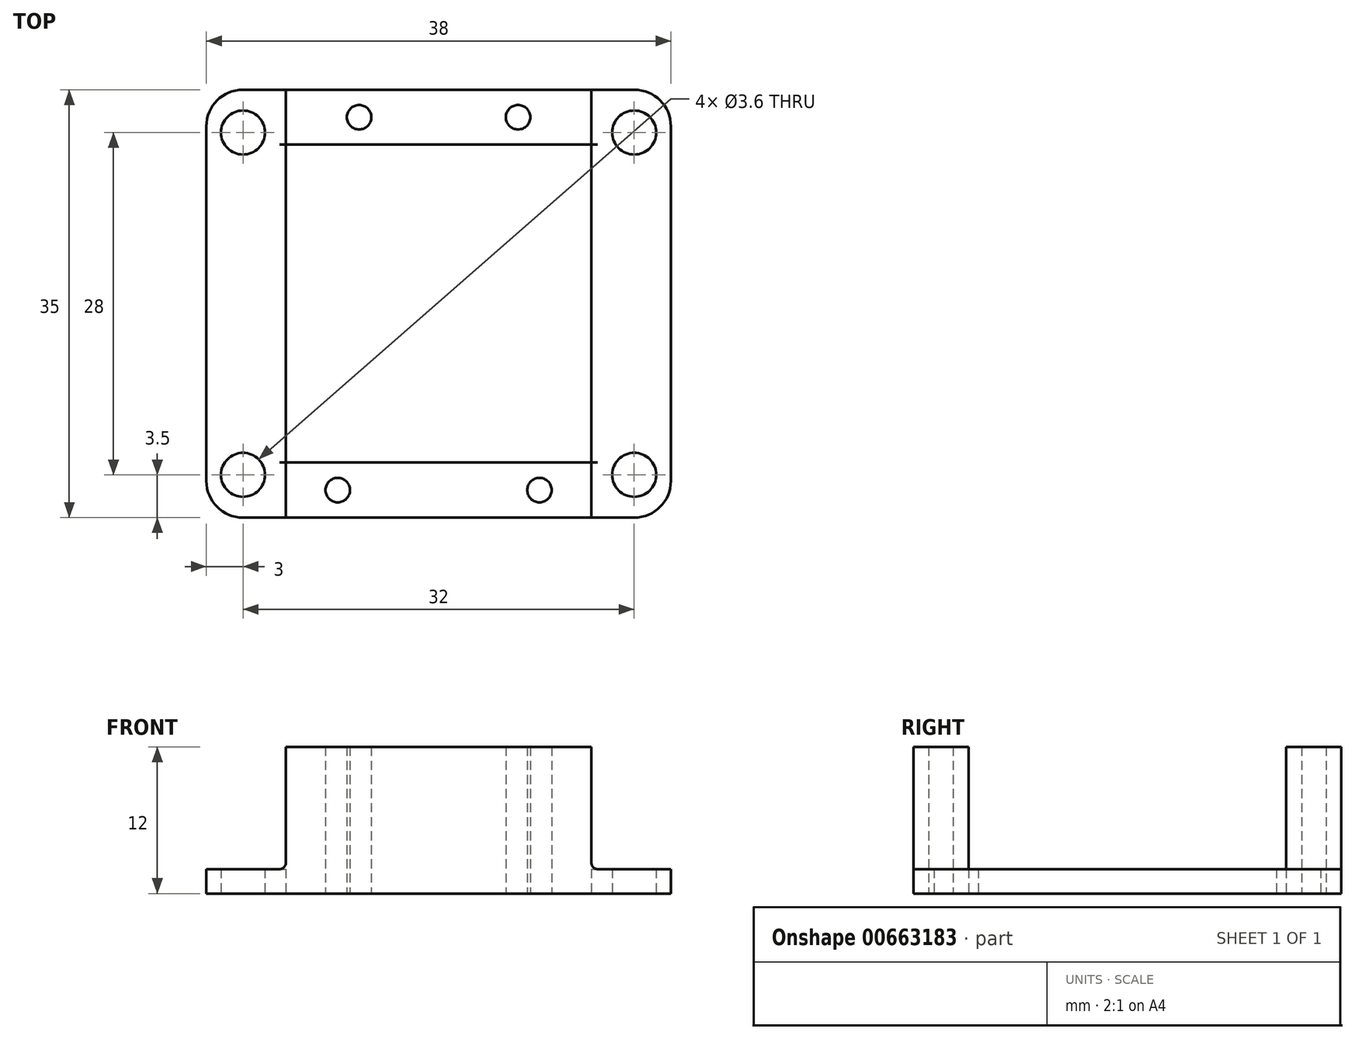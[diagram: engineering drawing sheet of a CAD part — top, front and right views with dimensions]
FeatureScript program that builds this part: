
annotation { "Feature Type Name" : "Feature", "Feature Type Description" : "" }
export const myFeature = defineFeature(function(context is Context, id is Id, definition is map)
    precondition{}
    {
        {
            var Q0;
            Q0=qCreatedBy(makeId("Top.planeOp"),FACE);
            var sketch = newSketch(context, id + "F0", { "sketchPlane" : qUnion([Q0])});
            skLineSegment(sketch, "E0.bottom", {"start": v(-19, 17.5) * mm, "end": v(19, 17.5) * mm});
            skLineSegment(sketch, "E0.top", {"start": v(-19, -17.5) * mm, "end": v(19, -17.5) * mm});
            skLineSegment(sketch, "E0.left", {"start": v(-19, 17.5) * mm, "end": v(-19, -17.5) * mm});
            skLineSegment(sketch, "E0.right", {"start": v(19, 17.5) * mm, "end": v(19, -17.5) * mm});
            skCircle(sketch, "E1", {"center": v(-16, 14) * mm, "radius": 1.8 * mm});
            skCircle(sketch, "E2.MirrorC", {"center": v(16, 14) * mm, "radius": 1.8 * mm});
            skCircle(sketch, "E3.MirrorC", {"center": v(-16, -14) * mm, "radius": 1.8 * mm});
            skCircle(sketch, "E4.MirrorC", {"center": v(16, -14) * mm, "radius": 1.8 * mm});
            skCircle(sketch, "E5", {"center": v(-6.5, 15.25) * mm, "radius": 1 * mm});
            skCircle(sketch, "E6.MirrorC", {"center": v(6.5, 15.25) * mm, "radius": 1 * mm});
            skCircle(sketch, "E7", {"center": v(-8.25, -15.25) * mm, "radius": 1 * mm});
            skCircle(sketch, "E8.MirrorC", {"center": v(8.25, -15.25) * mm, "radius": 1 * mm});
            skLineSegment(sketch, "E9", {"start": v(-6.5, 15.25) * mm, "end": v(6.5, 15.25) * mm, "construction": true});
            skLineSegment(sketch, "E10", {"start": v(-8.25, -15.25) * mm, "end": v(8.25, -15.25) * mm, "construction": true});
            skLineSegment(sketch, "E11", {"start": v(-12.5, 17.5) * mm, "end": v(-12.5, -17.5) * mm});
            skLineSegment(sketch, "E12", {"start": v(12.5, 17.5) * mm, "end": v(12.5, -17.5) * mm});
            skLineSegment(sketch, "E13", {"start": v(-12.5, 13) * mm, "end": v(12.5, 13) * mm});
            skLineSegment(sketch, "E14", {"start": v(-12.5, -13) * mm, "end": v(12.5, -13) * mm});
            skSolve(sketch);
        }
        {
            var Q0;
            {var subQ0=sQuery(id+"F0.wireOp",EDGE,"E0.left");Q0=makeQuery(id+"F0.imprint","IMPRINT",FACE,{"disambiguationData":[TD([[makeQuery(id+"F0.imprint","IMPRINT",EDGE,{"derivedFrom":subQ0}),1.0]])]});}
            var Q1;
            {var subQ3=sQuery(id+"F0.wireOp",EDGE,"E0.right");Q1=makeQuery(id+"F0.imprint","IMPRINT",FACE,{"disambiguationData":[TD([[makeQuery(id+"F0.imprint","IMPRINT",EDGE,{"derivedFrom":subQ3}),-1.0]])]});}
            var Q2;
            Q2=makeQuery(id+"F0.imprint","IMPRINT",FACE,{"disambiguationData":[TD([[makeQuery(id+"F0.imprint","IMPRINT",EDGE,{"derivedFrom":sQuery(id+"F0.wireOp",EDGE,"E5")}),-1.0]])]});
            var Q3;
            Q3=makeQuery(id+"F0.imprint","IMPRINT",FACE,{"disambiguationData":[TD([[makeQuery(id+"F0.imprint","IMPRINT",EDGE,{"derivedFrom":sQuery(id+"F0.wireOp",EDGE,"E7")}),-1.0]])]});
            extrude(context, id + "F1", {"entities" : qUnion([Q0, Q1, Q2, Q3]), "depth" : 2 * mm, "offsetDistance" : 25 * mm});
        }
        {
            var Q0;
            Q0=makeQuery(id+"F1.opExtrude","SWEPT_EDGE",EDGE,{"disambiguationData":[OSD([sQuery(id+"F0.wireOp",EDGE,"E0.bottom"),sQuery(id+"F0.wireOp",EDGE,"E0.left")])]});
            var Q1;
            Q1=makeQuery(id+"F1.opExtrude","SWEPT_EDGE",EDGE,{"disambiguationData":[OSD([sQuery(id+"F0.wireOp",EDGE,"E0.bottom"),sQuery(id+"F0.wireOp",EDGE,"E0.right")])]});
            var Q2;
            Q2=makeQuery(id+"F1.opExtrude","SWEPT_EDGE",EDGE,{"disambiguationData":[OSD([sQuery(id+"F0.wireOp",EDGE,"E0.top"),sQuery(id+"F0.wireOp",EDGE,"E0.right")])]});
            var Q3;
            Q3=makeQuery(id+"F1.opExtrude","SWEPT_EDGE",EDGE,{"disambiguationData":[OSD([sQuery(id+"F0.wireOp",EDGE,"E0.top"),sQuery(id+"F0.wireOp",EDGE,"E0.left")])]});
            fillet(context, id + "F2", {"entities" : qUnion([Q0, Q1, Q2, Q3]), "radius" : 3 * mm, "tangentPropagation" : true, "allowEdgeOverflow" : false});
        }
        {
            var Q0;
            Q0=makeQuery(id+"F0.imprint","IMPRINT",FACE,{"disambiguationData":[TD([[makeQuery(id+"F0.imprint","IMPRINT",EDGE,{"derivedFrom":sQuery(id+"F0.wireOp",EDGE,"E5")}),-1.0]])]});
            var Q1;
            Q1=makeQuery(id+"F0.imprint","IMPRINT",FACE,{"disambiguationData":[TD([[makeQuery(id+"F0.imprint","IMPRINT",EDGE,{"derivedFrom":sQuery(id+"F0.wireOp",EDGE,"E7")}),-1.0]])]});
            extrude(context, id + "F3", {"entities" : qUnion([Q0, Q1]), "operationType" : NewBodyOperationType.ADD, "depth" : 12 * mm, "offsetDistance" : 25 * mm});
        }
        {
            var Q0;
            {var subQ0=sQuery(id+"F0.wireOp",EDGE,"E11");var subQ1=sQuery(id+"F0.wireOp",EDGE,"E0.bottom");var subQ2=sQuery(id+"F0.wireOp",EDGE,"E13");Q0=makeQuery(id+"F3.boolean.opBoolean","INTERSECT",EDGE,{"derivedFrom":[makeQuery(id+"F1.opExtrude","CAP_FACE",FACE,{"disambiguationData":[OSD([subQ1,sQuery(id+"F0.wireOp",EDGE,"E0.top"),sQuery(id+"F0.wireOp",EDGE,"E0.left"),sQuery(id+"F0.wireOp",EDGE,"E0.right"),sQuery(id+"F0.wireOp",EDGE,"E1"),sQuery(id+"F0.wireOp",EDGE,"E2.MirrorC"),sQuery(id+"F0.wireOp",EDGE,"E3.MirrorC"),sQuery(id+"F0.wireOp",EDGE,"E4.MirrorC"),sQuery(id+"F0.wireOp",EDGE,"E5"),sQuery(id+"F0.wireOp",EDGE,"E6.MirrorC"),sQuery(id+"F0.wireOp",EDGE,"E7"),sQuery(id+"F0.wireOp",EDGE,"E8.MirrorC"),subQ0,sQuery(id+"F0.wireOp",EDGE,"E12"),subQ2,sQuery(id+"F0.wireOp",EDGE,"E14")])],"isStart":false}),makeQuery(id+"F3.opExtrude","SWEPT_FACE",FACE,{"disambiguationData":[OSD([subQ0]),TDD([makeQuery(id+"F0.imprint","IMPRINT",EDGE,{"disambiguationData":[TD([[makeQuery(id+"F0.imprint","INTERSECT",VERTEX,{"derivedFrom":[subQ1,subQ0]}),-1.0]])],"derivedFrom":subQ0})])]})]});}
            var Q1;
            {var subQ0=sQuery(id+"F0.wireOp",EDGE,"E11");var subQ1=sQuery(id+"F0.wireOp",EDGE,"E0.top");var subQ2=sQuery(id+"F0.wireOp",EDGE,"E14");Q1=makeQuery(id+"F3.boolean.opBoolean","INTERSECT",EDGE,{"derivedFrom":[makeQuery(id+"F1.opExtrude","CAP_FACE",FACE,{"disambiguationData":[OSD([sQuery(id+"F0.wireOp",EDGE,"E0.bottom"),subQ1,sQuery(id+"F0.wireOp",EDGE,"E0.left"),sQuery(id+"F0.wireOp",EDGE,"E0.right"),sQuery(id+"F0.wireOp",EDGE,"E1"),sQuery(id+"F0.wireOp",EDGE,"E2.MirrorC"),sQuery(id+"F0.wireOp",EDGE,"E3.MirrorC"),sQuery(id+"F0.wireOp",EDGE,"E4.MirrorC"),sQuery(id+"F0.wireOp",EDGE,"E5"),sQuery(id+"F0.wireOp",EDGE,"E6.MirrorC"),sQuery(id+"F0.wireOp",EDGE,"E7"),sQuery(id+"F0.wireOp",EDGE,"E8.MirrorC"),subQ0,sQuery(id+"F0.wireOp",EDGE,"E12"),sQuery(id+"F0.wireOp",EDGE,"E13"),subQ2])],"isStart":false}),makeQuery(id+"F3.opExtrude","SWEPT_FACE",FACE,{"disambiguationData":[OSD([subQ0]),TDD([makeQuery(id+"F0.imprint","IMPRINT",EDGE,{"disambiguationData":[TD([[makeQuery(id+"F0.imprint","INTERSECT",VERTEX,{"derivedFrom":[subQ1,subQ0]}),1.0]])],"derivedFrom":subQ0})])]})]});}
            var Q2;
            {var subQ0=sQuery(id+"F0.wireOp",EDGE,"E12");var subQ1=sQuery(id+"F0.wireOp",EDGE,"E0.bottom");var subQ2=sQuery(id+"F0.wireOp",EDGE,"E13");Q2=makeQuery(id+"F3.boolean.opBoolean","INTERSECT",EDGE,{"derivedFrom":[makeQuery(id+"F1.opExtrude","CAP_FACE",FACE,{"disambiguationData":[OSD([subQ1,sQuery(id+"F0.wireOp",EDGE,"E0.top"),sQuery(id+"F0.wireOp",EDGE,"E0.left"),sQuery(id+"F0.wireOp",EDGE,"E0.right"),sQuery(id+"F0.wireOp",EDGE,"E1"),sQuery(id+"F0.wireOp",EDGE,"E2.MirrorC"),sQuery(id+"F0.wireOp",EDGE,"E3.MirrorC"),sQuery(id+"F0.wireOp",EDGE,"E4.MirrorC"),sQuery(id+"F0.wireOp",EDGE,"E5"),sQuery(id+"F0.wireOp",EDGE,"E6.MirrorC"),sQuery(id+"F0.wireOp",EDGE,"E7"),sQuery(id+"F0.wireOp",EDGE,"E8.MirrorC"),sQuery(id+"F0.wireOp",EDGE,"E11"),subQ0,subQ2,sQuery(id+"F0.wireOp",EDGE,"E14")])],"isStart":false}),makeQuery(id+"F3.opExtrude","SWEPT_FACE",FACE,{"disambiguationData":[OSD([subQ0]),TDD([makeQuery(id+"F0.imprint","IMPRINT",EDGE,{"disambiguationData":[TD([[makeQuery(id+"F0.imprint","INTERSECT",VERTEX,{"derivedFrom":[subQ1,subQ0]}),-1.0]])],"derivedFrom":subQ0})])]})]});}
            var Q3;
            {var subQ0=sQuery(id+"F0.wireOp",EDGE,"E12");var subQ1=sQuery(id+"F0.wireOp",EDGE,"E0.top");var subQ2=sQuery(id+"F0.wireOp",EDGE,"E14");Q3=makeQuery(id+"F3.boolean.opBoolean","INTERSECT",EDGE,{"derivedFrom":[makeQuery(id+"F1.opExtrude","CAP_FACE",FACE,{"disambiguationData":[OSD([sQuery(id+"F0.wireOp",EDGE,"E0.bottom"),subQ1,sQuery(id+"F0.wireOp",EDGE,"E0.left"),sQuery(id+"F0.wireOp",EDGE,"E0.right"),sQuery(id+"F0.wireOp",EDGE,"E1"),sQuery(id+"F0.wireOp",EDGE,"E2.MirrorC"),sQuery(id+"F0.wireOp",EDGE,"E3.MirrorC"),sQuery(id+"F0.wireOp",EDGE,"E4.MirrorC"),sQuery(id+"F0.wireOp",EDGE,"E5"),sQuery(id+"F0.wireOp",EDGE,"E6.MirrorC"),sQuery(id+"F0.wireOp",EDGE,"E7"),sQuery(id+"F0.wireOp",EDGE,"E8.MirrorC"),sQuery(id+"F0.wireOp",EDGE,"E11"),subQ0,sQuery(id+"F0.wireOp",EDGE,"E13"),subQ2])],"isStart":false}),makeQuery(id+"F3.opExtrude","SWEPT_FACE",FACE,{"disambiguationData":[OSD([subQ0]),TDD([makeQuery(id+"F0.imprint","IMPRINT",EDGE,{"disambiguationData":[TD([[makeQuery(id+"F0.imprint","INTERSECT",VERTEX,{"derivedFrom":[subQ1,subQ0]}),1.0]])],"derivedFrom":subQ0})])]})]});}
            fillet(context, id + "F4", {"entities" : qUnion([Q0, Q1, Q2, Q3]), "radius" : 0.5 * mm, "tangentPropagation" : true, "allowEdgeOverflow" : false});
        }
    });
